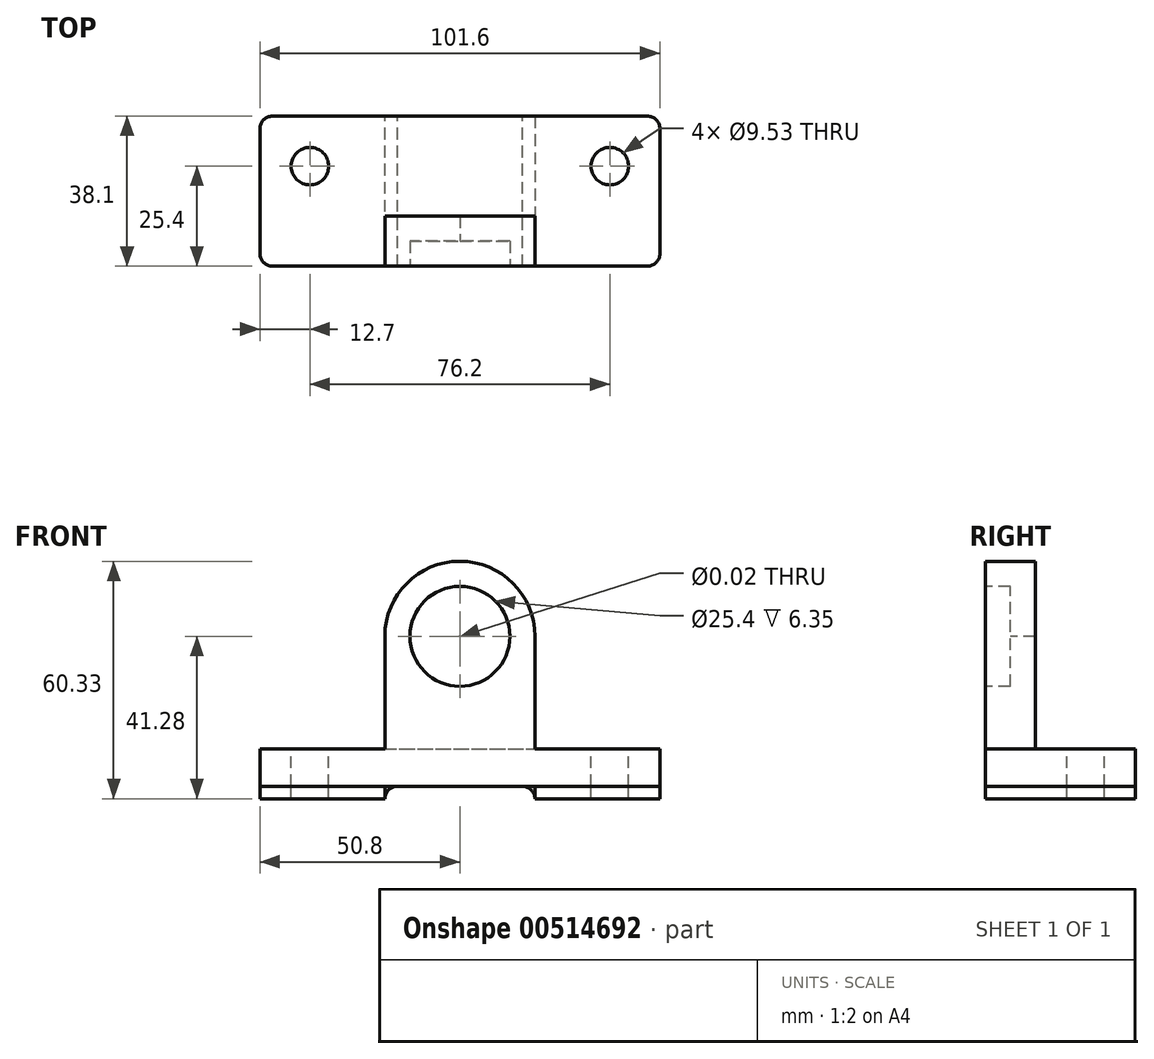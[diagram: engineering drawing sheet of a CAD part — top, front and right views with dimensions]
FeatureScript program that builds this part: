
annotation { "Feature Type Name" : "Feature", "Feature Type Description" : "" }
export const myFeature = defineFeature(function(context is Context, id is Id, definition is map)
    precondition{}
    {
        {
            var Q0;
            Q0=qCreatedBy(makeId("Top.planeOp"),FACE);
            var sketch = newSketch(context, id + "F0", { "sketchPlane" : qUnion([Q0])});
            skLineSegment(sketch, "E0.bottom", {"start": v(0, 0) * mm, "end": v(101.6, 0) * mm});
            skLineSegment(sketch, "E0.top", {"start": v(0, 38.1) * mm, "end": v(101.6, 38.1) * mm});
            skLineSegment(sketch, "E0.left", {"start": v(0, 0) * mm, "end": v(0, 38.1) * mm});
            skLineSegment(sketch, "E0.right", {"start": v(101.6, 0) * mm, "end": v(101.6, 38.1) * mm});
            skSolve(sketch);
        }
        {
            var Q0;
            Q0 = qSketchRegion(id + "F0", true);
            extrude(context, id + "F1", {"entities" : qUnion([Q0]), "depth" : 9.52 * mm, "offsetDistance" : 25.4 * mm});
        }
        {
            var Q0;
            Q0=makeQuery(id+"F1.opExtrude","SWEPT_FACE",FACE,{"disambiguationData":[OSD([sQuery(id+"F0.wireOp",EDGE,"E0.bottom")])]});
            var sketch = newSketch(context, id + "F2", { "sketchPlane" : qUnion([Q0])});
            skLineSegment(sketch, "E1", {"start": v(31.75, 0) * mm, "end": v(31.75, 38.1) * mm});
            skArc(sketch, "E2", {"start": v(69.85, 38.1) * mm, "mid": v(50.8, 57.15) * mm, "end": v(31.75, 38.1) * mm});
            skLineSegment(sketch, "E3", {"start": v(31.75, 38.1) * mm, "end": v(69.85, 38.1) * mm, "construction": true});
            skLineSegment(sketch, "E4", {"start": v(69.85, 38.1) * mm, "end": v(69.85, 0) * mm});
            skLineSegment(sketch, "E5", {"start": v(69.85, 0) * mm, "end": v(31.75, 0) * mm});
            skSolve(sketch);
        }
        {
            var Q0;
            Q0 = qSketchRegion(id + "F2", true);
            extrude(context, id + "F3", {"entities" : qUnion([Q0]), "operationType" : NewBodyOperationType.ADD, "oppositeDirection" : true, "depth" : 12.7 * mm, "offsetDistance" : 25.4 * mm});
        }
        {
            var Q0;
            Q0=makeQuery(id+"F3.boolean.opBoolean","MERGE",FACE,{"derivedFrom":[makeQuery(id+"F1.opExtrude","SWEPT_FACE",FACE,{"disambiguationData":[OSD([sQuery(id+"F0.wireOp",EDGE,"E0.bottom")])]}),makeQuery(id+"F3.opExtrude","CAP_FACE",FACE,{"disambiguationData":[OSD([sQuery(id+"F2.wireOp",EDGE,"E1"),sQuery(id+"F2.wireOp",EDGE,"E2"),sQuery(id+"F2.wireOp",EDGE,"E4"),sQuery(id+"F2.wireOp",EDGE,"E5")])],"isStart":true})]});
            var sketch = newSketch(context, id + "F4", { "sketchPlane" : qUnion([Q0])});
            skPoint(sketch, "E6", {"position": v(50.8, 38.1) * mm});
            skSolve(sketch);
        }
        {
            var Q0;
            Q0=sQuery(id+"F4.wireOp",VERTEX,"E6");
            var Q1;
            Q1=makeQuery(id+"F1.opExtrude","SWEPT_BODY",BODY,{"disambiguationData":[OSD([sQuery(id+"F0.wireOp",EDGE,"E0.bottom"),sQuery(id+"F0.wireOp",EDGE,"E0.top"),sQuery(id+"F0.wireOp",EDGE,"E0.left"),sQuery(id+"F0.wireOp",EDGE,"E0.right")])]});
            hole(context, id + "F5", {"style" : HoleStyle.C_BORE, "endStyle" : HoleEndStyle.THROUGH, "holeDiameter" : 15 / 812.8 * mm, "cBoreDiameter" : 25.4 * mm, "cBoreDepth" : 6.35 * mm, "isTappedThrough" : true, "tappedDepth" : 12.7 * mm, "tapClearance" : 3, "locations" : qUnion([Q0]), "scope" : qUnion([Q1])});
        }
        {
            var Q0;
            Q0=makeQuery(id+"F3.boolean.opBoolean","MERGE",FACE,{"derivedFrom":[makeQuery(id+"F1.opExtrude","SWEPT_FACE",FACE,{"disambiguationData":[OSD([sQuery(id+"F0.wireOp",EDGE,"E0.bottom")])]}),makeQuery(id+"F3.opExtrude","CAP_FACE",FACE,{"disambiguationData":[OSD([sQuery(id+"F2.wireOp",EDGE,"E1"),sQuery(id+"F2.wireOp",EDGE,"E2"),sQuery(id+"F2.wireOp",EDGE,"E4"),sQuery(id+"F2.wireOp",EDGE,"E5")])],"isStart":true})]});
            var sketch = newSketch(context, id + "F6", { "sketchPlane" : qUnion([Q0])});
            skLineSegment(sketch, "E7.bottom", {"start": v(31.75, 0) * mm, "end": v(69.85, 0) * mm});
            skLineSegment(sketch, "E7.top", {"start": v(31.75, 3.18) * mm, "end": v(69.85, 3.18) * mm});
            skLineSegment(sketch, "E7.left", {"start": v(31.75, 0) * mm, "end": v(31.75, 3.18) * mm});
            skLineSegment(sketch, "E7.right", {"start": v(69.85, 0) * mm, "end": v(69.85, 3.18) * mm});
            skSolve(sketch);
        }
        {
            var Q0;
            Q0=makeQuery(id+"F6.imprint","IMPRINT",FACE,{"disambiguationData":[TD([[makeQuery(id+"F6.imprint","IMPRINT",EDGE,{"derivedFrom":sQuery(id+"F6.wireOp",EDGE,"E7.top")}),1.0]])]});
            var sketch = newSketch(context, id + "F7", { "sketchPlane" : qUnion([Q0])});
            skLineSegment(sketch, "E8.bottom", {"start": v(0, 0) * mm, "end": v(31.75, 0) * mm});
            skLineSegment(sketch, "E8.top", {"start": v(0, -3.18) * mm, "end": v(31.75, -3.18) * mm});
            skLineSegment(sketch, "E8.left", {"start": v(0, 0) * mm, "end": v(0, -3.18) * mm});
            skLineSegment(sketch, "E8.right", {"start": v(31.75, 0) * mm, "end": v(31.75, -3.18) * mm});
            skLineSegment(sketch, "E9.bottom", {"start": v(69.85, 0) * mm, "end": v(101.6, 0) * mm});
            skLineSegment(sketch, "E9.top", {"start": v(69.85, -3.18) * mm, "end": v(101.6, -3.18) * mm});
            skLineSegment(sketch, "E9.left", {"start": v(69.85, 0) * mm, "end": v(69.85, -3.18) * mm});
            skLineSegment(sketch, "E9.right", {"start": v(101.6, 0) * mm, "end": v(101.6, -3.18) * mm});
            skSolve(sketch);
        }
        {
            var Q0;
            Q0 = qSketchRegion(id + "F7", true);
            var Q1;
            Q1=makeQuery(id+"F1.opExtrude","SWEPT_FACE",FACE,{"disambiguationData":[OSD([sQuery(id+"F0.wireOp",EDGE,"E0.top")])]});
            extrude(context, id + "F8", {"entities" : qUnion([Q0]), "endBound" : BoundingType.UP_TO_SURFACE, "oppositeDirection" : true, "depth" : 25.4 * mm, "endBoundEntityFace" : qUnion([Q1]), "offsetDistance" : 25.4 * mm});
        }
        {
            var Q0;
            Q0=makeQuery(id+"F1.opExtrude","CAP_FACE",FACE,{"disambiguationData":[OSD([sQuery(id+"F0.wireOp",EDGE,"E0.bottom"),sQuery(id+"F0.wireOp",EDGE,"E0.top"),sQuery(id+"F0.wireOp",EDGE,"E0.left"),sQuery(id+"F0.wireOp",EDGE,"E0.right")])],"isStart":false});
            var sketch = newSketch(context, id + "F9", { "sketchPlane" : qUnion([Q0])});
            skPoint(sketch, "E10", {"position": v(12.7, 25.4) * mm});
            skPoint(sketch, "E11", {"position": v(88.9, 25.4) * mm});
            skSolve(sketch);
        }
        {
            var Q0;
            Q0=sQuery(id+"F9.wireOp",VERTEX,"E10");
            var Q1;
            Q1=sQuery(id+"F9.wireOp",VERTEX,"E11");
            var Q2;
            Q2=makeQuery(id+"F1.opExtrude","SWEPT_BODY",BODY,{"disambiguationData":[OSD([sQuery(id+"F0.wireOp",EDGE,"E0.bottom"),sQuery(id+"F0.wireOp",EDGE,"E0.top"),sQuery(id+"F0.wireOp",EDGE,"E0.left"),sQuery(id+"F0.wireOp",EDGE,"E0.right")])]});
            var Q3;
            Q3=makeQuery(id+"F8.opExtrude","SWEPT_BODY",BODY,{"disambiguationData":[OSD([sQuery(id+"F7.wireOp",EDGE,"E8.bottom"),sQuery(id+"F7.wireOp",EDGE,"E8.top"),sQuery(id+"F7.wireOp",EDGE,"E8.left"),sQuery(id+"F7.wireOp",EDGE,"E8.right")])]});
            var Q4;
            Q4=makeQuery(id+"F8.opExtrude","SWEPT_BODY",BODY,{"disambiguationData":[OSD([sQuery(id+"F7.wireOp",EDGE,"E9.bottom"),sQuery(id+"F7.wireOp",EDGE,"E9.top"),sQuery(id+"F7.wireOp",EDGE,"E9.left"),sQuery(id+"F7.wireOp",EDGE,"E9.right")])]});
            hole(context, id + "F10", {"style" : HoleStyle.SIMPLE, "endStyle" : HoleEndStyle.THROUGH, "holeDiameter" : 9.52 * mm, "isTappedThrough" : true, "tappedDepth" : 12.7 * mm, "tapClearance" : 3, "locations" : qUnion([Q0, Q1]), "scope" : qUnion([Q2, Q3, Q4])});
        }
        {
            var Q0;
            Q0=makeQuery(id+"F1.opExtrude","SWEPT_EDGE",EDGE,{"disambiguationData":[OSD([sQuery(id+"F0.wireOp",EDGE,"E0.bottom"),sQuery(id+"F0.wireOp",EDGE,"E0.left")])]});
            var Q1;
            Q1=makeQuery(id+"F8.opExtrude","CAP_EDGE",EDGE,{"disambiguationData":[OSD([sQuery(id+"F7.wireOp",EDGE,"E8.left")])],"isStart":true});
            var Q2;
            Q2=makeQuery(id+"F1.opExtrude","SWEPT_EDGE",EDGE,{"disambiguationData":[OSD([sQuery(id+"F0.wireOp",EDGE,"E0.top"),sQuery(id+"F0.wireOp",EDGE,"E0.left")])]});
            var Q3;
            Q3=makeQuery(id+"F8.opExtrude","CAP_EDGE",EDGE,{"disambiguationData":[OSD([sQuery(id+"F7.wireOp",EDGE,"E8.left")])],"isStart":false});
            var Q4;
            Q4=makeQuery(id+"F1.opExtrude","SWEPT_EDGE",EDGE,{"disambiguationData":[OSD([sQuery(id+"F0.wireOp",EDGE,"E0.bottom"),sQuery(id+"F0.wireOp",EDGE,"E0.right")])]});
            var Q5;
            Q5=makeQuery(id+"F8.opExtrude","CAP_EDGE",EDGE,{"disambiguationData":[OSD([sQuery(id+"F7.wireOp",EDGE,"E9.right")])],"isStart":true});
            var Q6;
            Q6=makeQuery(id+"F1.opExtrude","SWEPT_EDGE",EDGE,{"disambiguationData":[OSD([sQuery(id+"F0.wireOp",EDGE,"E0.top"),sQuery(id+"F0.wireOp",EDGE,"E0.right")])]});
            var Q7;
            Q7=makeQuery(id+"F8.opExtrude","CAP_EDGE",EDGE,{"disambiguationData":[OSD([sQuery(id+"F7.wireOp",EDGE,"E9.right")])],"isStart":false});
            fillet(context, id + "F11", {"entities" : qUnion([Q0, Q1, Q2, Q3, Q4, Q5, Q6, Q7]), "radius" : 3.17 * mm, "tangentPropagation" : true, "allowEdgeOverflow" : false});
        }
        {
            var Q0;
            Q0=makeQuery(id+"F1.opExtrude","SWEPT_FACE",FACE,{"disambiguationData":[OSD([sQuery(id+"F0.wireOp",EDGE,"E0.top")])]});
            var sketch = newSketch(context, id + "F12", { "sketchPlane" : qUnion([Q0])});
            skArc(sketch, "E12", {"start": v(-34.92, 0) * mm, "mid": v(-32.68, -0.93) * mm, "end": v(-31.75, -3.18) * mm});
            skArc(sketch, "E13", {"start": v(-69.85, -3.17) * mm, "mid": v(-68.92, -0.93) * mm, "end": v(-66.68, 0) * mm});
            skLineSegment(sketch, "E14", {"start": v(-69.85, -3.17) * mm, "end": v(-69.85, 0) * mm});
            skLineSegment(sketch, "E15", {"start": v(-69.85, 0) * mm, "end": v(-66.68, 0) * mm});
            skLineSegment(sketch, "E16", {"start": v(-34.92, 0) * mm, "end": v(-31.73, 0) * mm});
            skLineSegment(sketch, "E17", {"start": v(-31.73, 0) * mm, "end": v(-31.75, -3.18) * mm});
            skSolve(sketch);
        }
        {
            var Q0;
            Q0 = qSketchRegion(id + "F12", true);
            var Q1;
            Q1=makeQuery(id+"F8.opExtrude","CAP_FACE",FACE,{"disambiguationData":[OSD([sQuery(id+"F7.wireOp",EDGE,"E8.bottom"),sQuery(id+"F7.wireOp",EDGE,"E8.top"),sQuery(id+"F7.wireOp",EDGE,"E8.left"),sQuery(id+"F7.wireOp",EDGE,"E8.right")])],"isStart":true});
            extrude(context, id + "F13", {"entities" : qUnion([Q0]), "endBound" : BoundingType.UP_TO_SURFACE, "oppositeDirection" : true, "depth" : 25.4 * mm, "endBoundEntityFace" : qUnion([Q1]), "offsetDistance" : 25.4 * mm});
        }
    });
